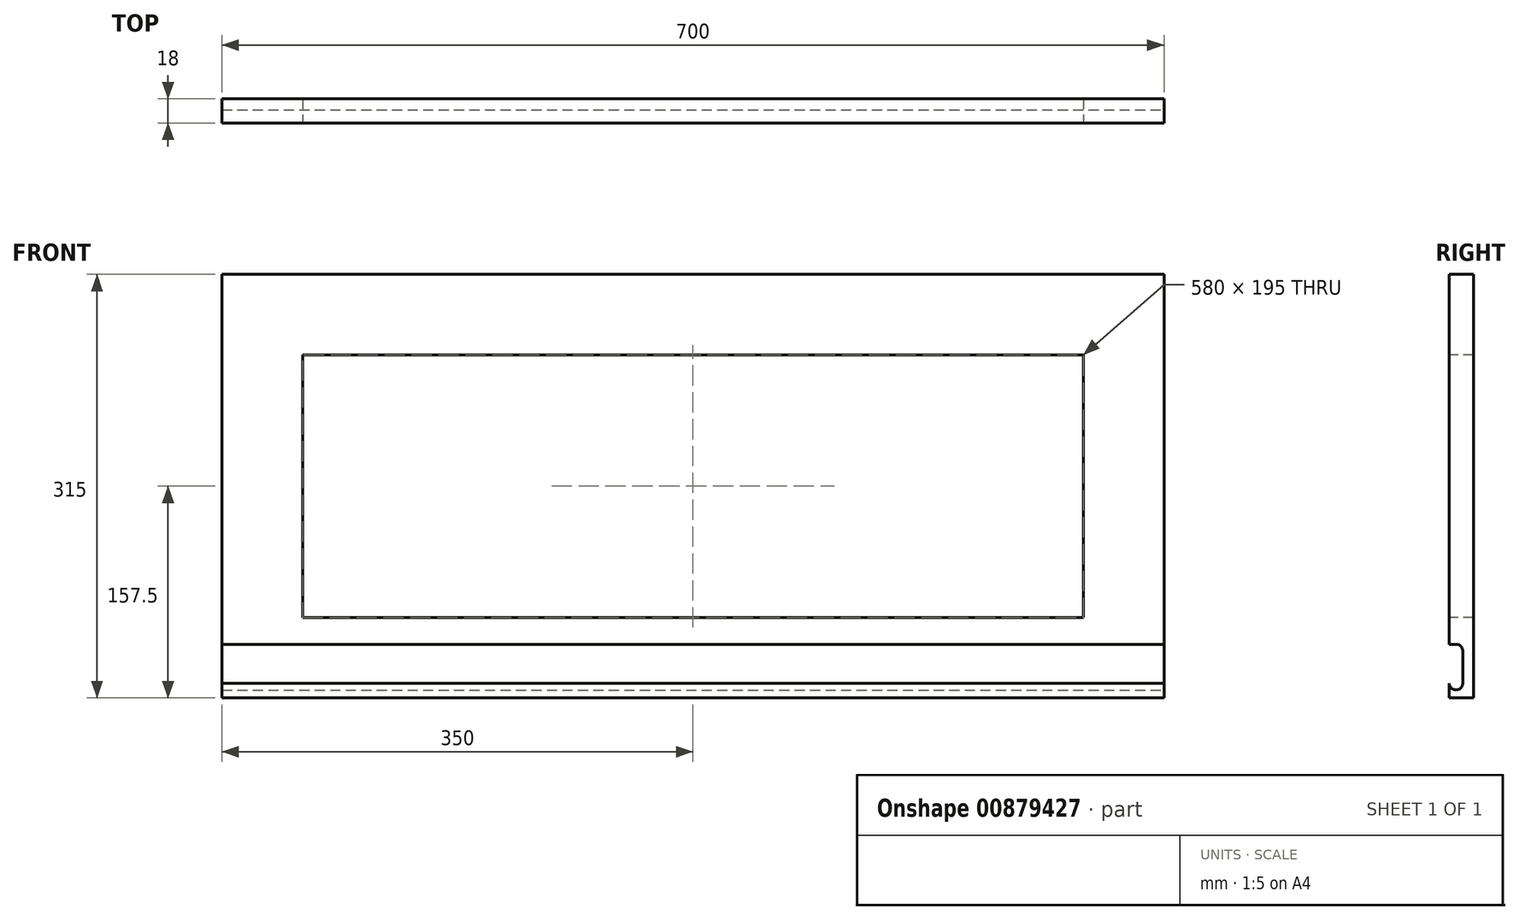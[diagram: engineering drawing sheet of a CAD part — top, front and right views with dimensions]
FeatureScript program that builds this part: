
annotation { "Feature Type Name" : "Feature", "Feature Type Description" : "" }
export const myFeature = defineFeature(function(context is Context, id is Id, definition is map)
    precondition{}
    {
        {
            var Q0;
            Q0=qCreatedBy(makeId("Front.planeOp"),FACE);
            var sketch = newSketch(context, id + "F0", { "sketchPlane" : qUnion([Q0])});
            skLineSegment(sketch, "E0.top", {"start": v(0, 0) * mm, "end": v(700, 0) * mm});
            skLineSegment(sketch, "E1", {"start": v(0, 0) * mm, "end": v(0, 315) * mm});
            skLineSegment(sketch, "E2", {"start": v(700, 0) * mm, "end": v(700, 315) * mm});
            skLineSegment(sketch, "E3", {"start": v(0, 315) * mm, "end": v(700, 315) * mm});
            skLineSegment(sketch, "E4.0", {"start": v(60, 60) * mm, "end": v(640, 60) * mm});
            skLineSegment(sketch, "E4.1", {"start": v(60, 60) * mm, "end": v(60, 255) * mm});
            skLineSegment(sketch, "E4.2", {"start": v(60, 255) * mm, "end": v(640, 255) * mm});
            skLineSegment(sketch, "E4.3", {"start": v(640, 60) * mm, "end": v(640, 255) * mm});
            skSolve(sketch);
        }
        {
            var Q0;
            Q0=makeQuery(id+"F0.imprint","IMPRINT",FACE,{"disambiguationData":[TD([[makeQuery(id+"F0.imprint","IMPRINT",EDGE,{"derivedFrom":sQuery(id+"F0.wireOp",EDGE,"E0.top")}),1.0]])]});
            extrude(context, id + "F1", {"entities" : qUnion([Q0]), "oppositeDirection" : true, "depth" : 18 * mm, "offsetDistance" : 25 * mm});
        }
        {
            var Q0;
            Q0=makeQuery(id+"F1.opExtrude","SWEPT_FACE",FACE,{"disambiguationData":[OSD([sQuery(id+"F0.wireOp",EDGE,"E2")])]});
            var sketch = newSketch(context, id + "F2", { "sketchPlane" : qUnion([Q0])});
            skLineSegment(sketch, "E5", {"start": v(0, 40) * mm, "end": v(5, 40) * mm});
            skLineSegment(sketch, "E6", {"start": v(10, 35) * mm, "end": v(10, 11) * mm});
            skArc(sketch, "E7", {"start": v(0, 11) * mm, "mid": v(5, 6) * mm, "end": v(10, 11) * mm});
            skPoint(sketch, "E8.visualSharp", {"position": v(10, 40) * mm});
            skArc(sketch, "E8.filletArc", {"start": v(10, 35) * mm, "mid": v(8.54, 38.54) * mm, "end": v(5, 40) * mm});
            skSolve(sketch);
        }
        {
            var Q0;
            {var subQ1=sQuery(id+"F2.wireOp",EDGE,"E5");Q0=makeQuery(id+"F2.imprint","IMPRINT",FACE,{"disambiguationData":[TD([[makeQuery(id+"F2.imprint","IMPRINT",EDGE,{"derivedFrom":subQ1}),-1.0]])]});}
            extrude(context, id + "F3", {"entities" : qUnion([Q0]), "operationType" : NewBodyOperationType.REMOVE, "oppositeDirection" : true, "depth" : 940 * mm, "offsetDistance" : 25 * mm});
        }
    });
